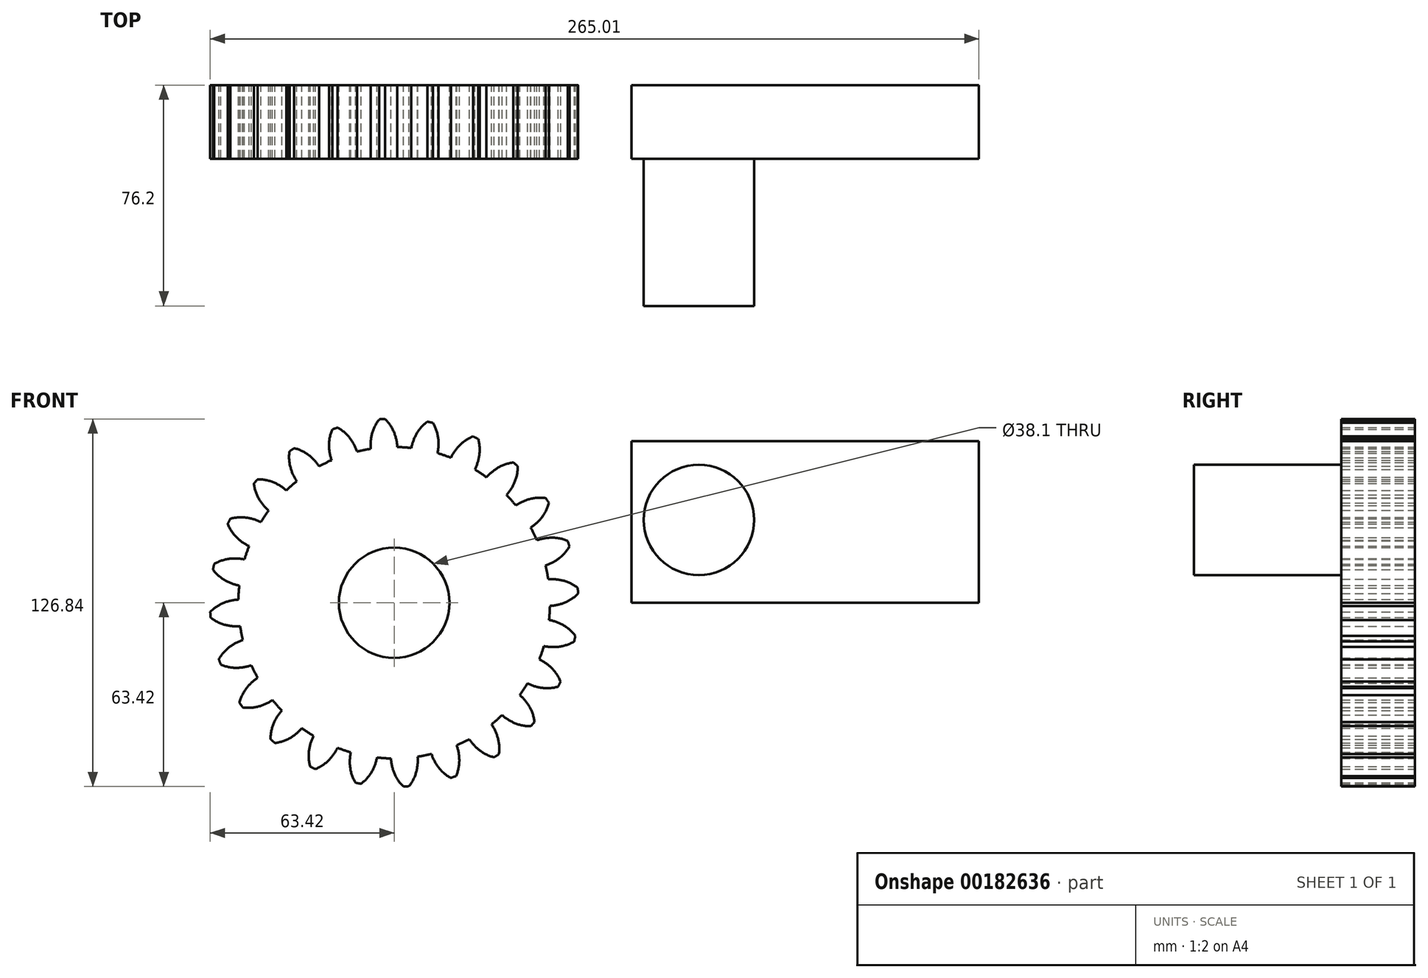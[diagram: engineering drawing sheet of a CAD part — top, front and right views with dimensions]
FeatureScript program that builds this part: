
annotation { "Feature Type Name" : "Feature", "Feature Type Description" : "" }
export const myFeature = defineFeature(function(context is Context, id is Id, definition is map)
    precondition{}
    {
        {
            var Q0;
            Q0=qCreatedBy(makeId("Front.planeOp"),FACE);
            var sketch = newSketch(context, id + "F0", { "sketchPlane" : qUnion([Q0])});
            skCircle(sketch, "E0", {"center": v(0, 0) * mm, "radius": 63.5 * mm, "construction": true});
            skCircle(sketch, "E1", {"center": v(0, 0) * mm, "radius": 58.67 * mm, "construction": true});
            skCircle(sketch, "E2", {"center": v(0, 0) * mm, "radius": 53.72 * mm});
            skLineSegment(sketch, "E3", {"start": v(0, 0) * mm, "end": v(0, 93.27) * mm, "construction": true});
            skLineSegment(sketch, "E4", {"start": v(0, 0) * mm, "end": v(-6.11, 93.27) * mm, "construction": true});
            skLineSegment(sketch, "E5", {"start": v(0, 58.67) * mm, "end": v(-115.99, 14.2) * mm, "construction": true});
            skLineSegment(sketch, "E6", {"start": v(-49.6, 39.66) * mm, "end": v(0, 58.67) * mm, "construction": true});
            skLineSegment(sketch, "E7", {"start": v(0, 58.67) * mm, "end": v(-118.86, 56.64) * mm, "construction": true});
            skCircle(sketch, "E8", {"center": v(0, 0) * mm, "radius": 54.78 * mm, "construction": true});
            skCircle(sketch, "E9", {"center": v(0, 58.67) * mm, "radius": 14.6 * mm, "construction": true});
            skCircle(sketch, "E10", {"center": v(-13.5, 53.1) * mm, "radius": 14.6 * mm, "construction": true});
            skArc(sketch, "E11", {"start": v(0, 58.67) * mm, "mid": v(-1.34, 61.21) * mm, "end": v(-3.17, 63.42) * mm});
            skArc(sketch, "E12", {"start": v(1.1, 53.7) * mm, "mid": v(0.75, 56.24) * mm, "end": v(0, 58.67) * mm});
            skArc(sketch, "E13.MirrorCS", {"start": v(-7.66, 58.17) * mm, "mid": v(-6.67, 60.86) * mm, "end": v(-5.14, 63.3) * mm});
            skArc(sketch, "E14.MirrorCS", {"start": v(-8.1, 53.1) * mm, "mid": v(-8.08, 55.66) * mm, "end": v(-7.66, 58.17) * mm});
            skArc(sketch, "E15", {"start": v(-3.17, 63.42) * mm, "mid": v(-4.15, 63.36) * mm, "end": v(-5.14, 63.3) * mm});
            skSolve(sketch);
        }
        {
            var Q0;
            {var subQ0=sQuery(id+"F0.wireOp",EDGE,"E2");var subQ1=makeQuery(id+"F0.imprint","INTERSECT",VERTEX,{"derivedFrom":[subQ0,sQuery(id+"F0.wireOp",EDGE,"E12")]});Q0=makeQuery(id+"F0.imprint","IMPRINT",FACE,{"disambiguationData":[TD([[makeQuery(id+"F0.imprint","IMPRINT",EDGE,{"disambiguationData":[TD([[subQ1,-1.0]])],"derivedFrom":subQ0}),1.0]])]});}
            var Q1;
            Q1=makeQuery(id+"F0.imprint","IMPRINT",FACE,{"disambiguationData":[TD([[makeQuery(id+"F0.imprint","IMPRINT",EDGE,{"derivedFrom":sQuery(id+"F0.wireOp",EDGE,"E11")}),1.0]])]});
            extrude(context, id + "F1", {"entities" : qUnion([Q0, Q1]), "depth" : 25.4 * mm});
        }
        {
            var Q0;
            Q0=makeQuery(id+"F1.opExtrude","SWEPT_BODY",BODY,{"disambiguationData":[OSD([sQuery(id+"F0.wireOp",EDGE,"E2"),sQuery(id+"F0.wireOp",EDGE,"E11"),sQuery(id+"F0.wireOp",EDGE,"E12"),sQuery(id+"F0.wireOp",EDGE,"E13.MirrorCS"),sQuery(id+"F0.wireOp",EDGE,"E14.MirrorCS"),sQuery(id+"F0.wireOp",EDGE,"E15")])]});
            var Q1;
            Q1=makeQuery(id+"F1.opExtrude","SWEPT_FACE",FACE,{"disambiguationData":[OSD([sQuery(id+"F0.wireOp",EDGE,"E2")])]});
            circularPattern(context, id + "F2", {"entities" : qUnion([Q0]), "axis" : qUnion([Q1]), "angle" : 15 * degree, "instanceCount" : 24});
        }
        {
            var Q0;
            Q0=makeQuery(id+"F2.opPattern","COPY",BODY,{"derivedFrom":makeQuery(id+"F1.opExtrude","SWEPT_BODY",BODY,{"disambiguationData":[OSD([sQuery(id+"F0.wireOp",EDGE,"E2"),sQuery(id+"F0.wireOp",EDGE,"E11"),sQuery(id+"F0.wireOp",EDGE,"E12"),sQuery(id+"F0.wireOp",EDGE,"E13.MirrorCS"),sQuery(id+"F0.wireOp",EDGE,"E14.MirrorCS"),sQuery(id+"F0.wireOp",EDGE,"E15")])]}),"instanceName":"9"});
            var Q1;
            Q1=makeQuery(id+"F2.opPattern","COPY",BODY,{"derivedFrom":makeQuery(id+"F1.opExtrude","SWEPT_BODY",BODY,{"disambiguationData":[OSD([sQuery(id+"F0.wireOp",EDGE,"E2"),sQuery(id+"F0.wireOp",EDGE,"E11"),sQuery(id+"F0.wireOp",EDGE,"E12"),sQuery(id+"F0.wireOp",EDGE,"E13.MirrorCS"),sQuery(id+"F0.wireOp",EDGE,"E14.MirrorCS"),sQuery(id+"F0.wireOp",EDGE,"E15")])]}),"instanceName":"23"});
            var Q2;
            Q2=makeQuery(id+"F2.opPattern","COPY",BODY,{"derivedFrom":makeQuery(id+"F1.opExtrude","SWEPT_BODY",BODY,{"disambiguationData":[OSD([sQuery(id+"F0.wireOp",EDGE,"E2"),sQuery(id+"F0.wireOp",EDGE,"E11"),sQuery(id+"F0.wireOp",EDGE,"E12"),sQuery(id+"F0.wireOp",EDGE,"E13.MirrorCS"),sQuery(id+"F0.wireOp",EDGE,"E14.MirrorCS"),sQuery(id+"F0.wireOp",EDGE,"E15")])]}),"instanceName":"22"});
            var Q3;
            Q3=makeQuery(id+"F2.opPattern","COPY",BODY,{"derivedFrom":makeQuery(id+"F1.opExtrude","SWEPT_BODY",BODY,{"disambiguationData":[OSD([sQuery(id+"F0.wireOp",EDGE,"E2"),sQuery(id+"F0.wireOp",EDGE,"E11"),sQuery(id+"F0.wireOp",EDGE,"E12"),sQuery(id+"F0.wireOp",EDGE,"E13.MirrorCS"),sQuery(id+"F0.wireOp",EDGE,"E14.MirrorCS"),sQuery(id+"F0.wireOp",EDGE,"E15")])]}),"instanceName":"21"});
            var Q4;
            Q4=makeQuery(id+"F2.opPattern","COPY",BODY,{"derivedFrom":makeQuery(id+"F1.opExtrude","SWEPT_BODY",BODY,{"disambiguationData":[OSD([sQuery(id+"F0.wireOp",EDGE,"E2"),sQuery(id+"F0.wireOp",EDGE,"E11"),sQuery(id+"F0.wireOp",EDGE,"E12"),sQuery(id+"F0.wireOp",EDGE,"E13.MirrorCS"),sQuery(id+"F0.wireOp",EDGE,"E14.MirrorCS"),sQuery(id+"F0.wireOp",EDGE,"E15")])]}),"instanceName":"20"});
            var Q5;
            Q5=makeQuery(id+"F2.opPattern","COPY",BODY,{"derivedFrom":makeQuery(id+"F1.opExtrude","SWEPT_BODY",BODY,{"disambiguationData":[OSD([sQuery(id+"F0.wireOp",EDGE,"E2"),sQuery(id+"F0.wireOp",EDGE,"E11"),sQuery(id+"F0.wireOp",EDGE,"E12"),sQuery(id+"F0.wireOp",EDGE,"E13.MirrorCS"),sQuery(id+"F0.wireOp",EDGE,"E14.MirrorCS"),sQuery(id+"F0.wireOp",EDGE,"E15")])]}),"instanceName":"16"});
            var Q6;
            Q6=makeQuery(id+"F2.opPattern","COPY",BODY,{"derivedFrom":makeQuery(id+"F1.opExtrude","SWEPT_BODY",BODY,{"disambiguationData":[OSD([sQuery(id+"F0.wireOp",EDGE,"E2"),sQuery(id+"F0.wireOp",EDGE,"E11"),sQuery(id+"F0.wireOp",EDGE,"E12"),sQuery(id+"F0.wireOp",EDGE,"E13.MirrorCS"),sQuery(id+"F0.wireOp",EDGE,"E14.MirrorCS"),sQuery(id+"F0.wireOp",EDGE,"E15")])]}),"instanceName":"18"});
            var Q7;
            Q7=makeQuery(id+"F2.opPattern","COPY",BODY,{"derivedFrom":makeQuery(id+"F1.opExtrude","SWEPT_BODY",BODY,{"disambiguationData":[OSD([sQuery(id+"F0.wireOp",EDGE,"E2"),sQuery(id+"F0.wireOp",EDGE,"E11"),sQuery(id+"F0.wireOp",EDGE,"E12"),sQuery(id+"F0.wireOp",EDGE,"E13.MirrorCS"),sQuery(id+"F0.wireOp",EDGE,"E14.MirrorCS"),sQuery(id+"F0.wireOp",EDGE,"E15")])]}),"instanceName":"17"});
            var Q8;
            Q8=makeQuery(id+"F2.opPattern","COPY",BODY,{"derivedFrom":makeQuery(id+"F1.opExtrude","SWEPT_BODY",BODY,{"disambiguationData":[OSD([sQuery(id+"F0.wireOp",EDGE,"E2"),sQuery(id+"F0.wireOp",EDGE,"E11"),sQuery(id+"F0.wireOp",EDGE,"E12"),sQuery(id+"F0.wireOp",EDGE,"E13.MirrorCS"),sQuery(id+"F0.wireOp",EDGE,"E14.MirrorCS"),sQuery(id+"F0.wireOp",EDGE,"E15")])]}),"instanceName":"19"});
            var Q9;
            Q9=makeQuery(id+"F2.opPattern","COPY",BODY,{"derivedFrom":makeQuery(id+"F1.opExtrude","SWEPT_BODY",BODY,{"disambiguationData":[OSD([sQuery(id+"F0.wireOp",EDGE,"E2"),sQuery(id+"F0.wireOp",EDGE,"E11"),sQuery(id+"F0.wireOp",EDGE,"E12"),sQuery(id+"F0.wireOp",EDGE,"E13.MirrorCS"),sQuery(id+"F0.wireOp",EDGE,"E14.MirrorCS"),sQuery(id+"F0.wireOp",EDGE,"E15")])]}),"instanceName":"15"});
            var Q10;
            Q10=makeQuery(id+"F2.opPattern","COPY",BODY,{"derivedFrom":makeQuery(id+"F1.opExtrude","SWEPT_BODY",BODY,{"disambiguationData":[OSD([sQuery(id+"F0.wireOp",EDGE,"E2"),sQuery(id+"F0.wireOp",EDGE,"E11"),sQuery(id+"F0.wireOp",EDGE,"E12"),sQuery(id+"F0.wireOp",EDGE,"E13.MirrorCS"),sQuery(id+"F0.wireOp",EDGE,"E14.MirrorCS"),sQuery(id+"F0.wireOp",EDGE,"E15")])]}),"instanceName":"14"});
            var Q11;
            Q11=makeQuery(id+"F2.opPattern","COPY",BODY,{"derivedFrom":makeQuery(id+"F1.opExtrude","SWEPT_BODY",BODY,{"disambiguationData":[OSD([sQuery(id+"F0.wireOp",EDGE,"E2"),sQuery(id+"F0.wireOp",EDGE,"E11"),sQuery(id+"F0.wireOp",EDGE,"E12"),sQuery(id+"F0.wireOp",EDGE,"E13.MirrorCS"),sQuery(id+"F0.wireOp",EDGE,"E14.MirrorCS"),sQuery(id+"F0.wireOp",EDGE,"E15")])]}),"instanceName":"12"});
            var Q12;
            Q12=makeQuery(id+"F2.opPattern","COPY",BODY,{"derivedFrom":makeQuery(id+"F1.opExtrude","SWEPT_BODY",BODY,{"disambiguationData":[OSD([sQuery(id+"F0.wireOp",EDGE,"E2"),sQuery(id+"F0.wireOp",EDGE,"E11"),sQuery(id+"F0.wireOp",EDGE,"E12"),sQuery(id+"F0.wireOp",EDGE,"E13.MirrorCS"),sQuery(id+"F0.wireOp",EDGE,"E14.MirrorCS"),sQuery(id+"F0.wireOp",EDGE,"E15")])]}),"instanceName":"13"});
            var Q13;
            Q13=makeQuery(id+"F2.opPattern","COPY",BODY,{"derivedFrom":makeQuery(id+"F1.opExtrude","SWEPT_BODY",BODY,{"disambiguationData":[OSD([sQuery(id+"F0.wireOp",EDGE,"E2"),sQuery(id+"F0.wireOp",EDGE,"E11"),sQuery(id+"F0.wireOp",EDGE,"E12"),sQuery(id+"F0.wireOp",EDGE,"E13.MirrorCS"),sQuery(id+"F0.wireOp",EDGE,"E14.MirrorCS"),sQuery(id+"F0.wireOp",EDGE,"E15")])]}),"instanceName":"11"});
            var Q14;
            Q14=makeQuery(id+"F2.opPattern","COPY",BODY,{"derivedFrom":makeQuery(id+"F1.opExtrude","SWEPT_BODY",BODY,{"disambiguationData":[OSD([sQuery(id+"F0.wireOp",EDGE,"E2"),sQuery(id+"F0.wireOp",EDGE,"E11"),sQuery(id+"F0.wireOp",EDGE,"E12"),sQuery(id+"F0.wireOp",EDGE,"E13.MirrorCS"),sQuery(id+"F0.wireOp",EDGE,"E14.MirrorCS"),sQuery(id+"F0.wireOp",EDGE,"E15")])]}),"instanceName":"10"});
            var Q15;
            Q15=makeQuery(id+"F2.opPattern","COPY",BODY,{"derivedFrom":makeQuery(id+"F1.opExtrude","SWEPT_BODY",BODY,{"disambiguationData":[OSD([sQuery(id+"F0.wireOp",EDGE,"E2"),sQuery(id+"F0.wireOp",EDGE,"E11"),sQuery(id+"F0.wireOp",EDGE,"E12"),sQuery(id+"F0.wireOp",EDGE,"E13.MirrorCS"),sQuery(id+"F0.wireOp",EDGE,"E14.MirrorCS"),sQuery(id+"F0.wireOp",EDGE,"E15")])]}),"instanceName":"8"});
            var Q16;
            Q16=makeQuery(id+"F2.opPattern","COPY",BODY,{"derivedFrom":makeQuery(id+"F1.opExtrude","SWEPT_BODY",BODY,{"disambiguationData":[OSD([sQuery(id+"F0.wireOp",EDGE,"E2"),sQuery(id+"F0.wireOp",EDGE,"E11"),sQuery(id+"F0.wireOp",EDGE,"E12"),sQuery(id+"F0.wireOp",EDGE,"E13.MirrorCS"),sQuery(id+"F0.wireOp",EDGE,"E14.MirrorCS"),sQuery(id+"F0.wireOp",EDGE,"E15")])]}),"instanceName":"7"});
            var Q17;
            Q17=makeQuery(id+"F2.opPattern","COPY",BODY,{"derivedFrom":makeQuery(id+"F1.opExtrude","SWEPT_BODY",BODY,{"disambiguationData":[OSD([sQuery(id+"F0.wireOp",EDGE,"E2"),sQuery(id+"F0.wireOp",EDGE,"E11"),sQuery(id+"F0.wireOp",EDGE,"E12"),sQuery(id+"F0.wireOp",EDGE,"E13.MirrorCS"),sQuery(id+"F0.wireOp",EDGE,"E14.MirrorCS"),sQuery(id+"F0.wireOp",EDGE,"E15")])]}),"instanceName":"6"});
            var Q18;
            Q18=makeQuery(id+"F2.opPattern","COPY",BODY,{"derivedFrom":makeQuery(id+"F1.opExtrude","SWEPT_BODY",BODY,{"disambiguationData":[OSD([sQuery(id+"F0.wireOp",EDGE,"E2"),sQuery(id+"F0.wireOp",EDGE,"E11"),sQuery(id+"F0.wireOp",EDGE,"E12"),sQuery(id+"F0.wireOp",EDGE,"E13.MirrorCS"),sQuery(id+"F0.wireOp",EDGE,"E14.MirrorCS"),sQuery(id+"F0.wireOp",EDGE,"E15")])]}),"instanceName":"5"});
            var Q19;
            Q19=makeQuery(id+"F2.opPattern","COPY",BODY,{"derivedFrom":makeQuery(id+"F1.opExtrude","SWEPT_BODY",BODY,{"disambiguationData":[OSD([sQuery(id+"F0.wireOp",EDGE,"E2"),sQuery(id+"F0.wireOp",EDGE,"E11"),sQuery(id+"F0.wireOp",EDGE,"E12"),sQuery(id+"F0.wireOp",EDGE,"E13.MirrorCS"),sQuery(id+"F0.wireOp",EDGE,"E14.MirrorCS"),sQuery(id+"F0.wireOp",EDGE,"E15")])]}),"instanceName":"4"});
            var Q20;
            Q20=makeQuery(id+"F2.opPattern","COPY",BODY,{"derivedFrom":makeQuery(id+"F1.opExtrude","SWEPT_BODY",BODY,{"disambiguationData":[OSD([sQuery(id+"F0.wireOp",EDGE,"E2"),sQuery(id+"F0.wireOp",EDGE,"E11"),sQuery(id+"F0.wireOp",EDGE,"E12"),sQuery(id+"F0.wireOp",EDGE,"E13.MirrorCS"),sQuery(id+"F0.wireOp",EDGE,"E14.MirrorCS"),sQuery(id+"F0.wireOp",EDGE,"E15")])]}),"instanceName":"2"});
            var Q21;
            Q21=makeQuery(id+"F2.opPattern","COPY",BODY,{"derivedFrom":makeQuery(id+"F1.opExtrude","SWEPT_BODY",BODY,{"disambiguationData":[OSD([sQuery(id+"F0.wireOp",EDGE,"E2"),sQuery(id+"F0.wireOp",EDGE,"E11"),sQuery(id+"F0.wireOp",EDGE,"E12"),sQuery(id+"F0.wireOp",EDGE,"E13.MirrorCS"),sQuery(id+"F0.wireOp",EDGE,"E14.MirrorCS"),sQuery(id+"F0.wireOp",EDGE,"E15")])]}),"instanceName":"3"});
            var Q22;
            Q22=makeQuery(id+"F2.opPattern","COPY",BODY,{"derivedFrom":makeQuery(id+"F1.opExtrude","SWEPT_BODY",BODY,{"disambiguationData":[OSD([sQuery(id+"F0.wireOp",EDGE,"E2"),sQuery(id+"F0.wireOp",EDGE,"E11"),sQuery(id+"F0.wireOp",EDGE,"E12"),sQuery(id+"F0.wireOp",EDGE,"E13.MirrorCS"),sQuery(id+"F0.wireOp",EDGE,"E14.MirrorCS"),sQuery(id+"F0.wireOp",EDGE,"E15")])]}),"instanceName":"1"});
            var Q23;
            Q23=makeQuery(id+"F1.opExtrude","SWEPT_BODY",BODY,{"disambiguationData":[OSD([sQuery(id+"F0.wireOp",EDGE,"E2"),sQuery(id+"F0.wireOp",EDGE,"E11"),sQuery(id+"F0.wireOp",EDGE,"E12"),sQuery(id+"F0.wireOp",EDGE,"E13.MirrorCS"),sQuery(id+"F0.wireOp",EDGE,"E14.MirrorCS"),sQuery(id+"F0.wireOp",EDGE,"E15")])]});
            booleanBodies(context, id + "F3", {"operationType" : BooleanOperationType.UNION, "tools" : qUnion([Q0, Q1, Q2, Q3, Q4, Q5, Q6, Q7, Q8, Q9, Q10, Q11, Q12, Q13, Q14, Q15, Q16, Q17, Q18, Q19, Q20, Q21, Q22, Q23])});
        }
        {
            var Q0;
            {var subQ0=makeQuery(id+"F1.opExtrude","CAP_FACE",FACE,{"disambiguationData":[OSD([sQuery(id+"F0.wireOp",EDGE,"E2"),sQuery(id+"F0.wireOp",EDGE,"E11"),sQuery(id+"F0.wireOp",EDGE,"E12"),sQuery(id+"F0.wireOp",EDGE,"E13.MirrorCS"),sQuery(id+"F0.wireOp",EDGE,"E14.MirrorCS"),sQuery(id+"F0.wireOp",EDGE,"E15")])],"isStart":true});Q0=makeQuery(id+"F3.opBoolean","MERGE",FACE,{"derivedFrom":[subQ0,makeQuery(id+"F2.opPattern","COPY",FACE,{"derivedFrom":subQ0,"instanceName":"1"}),makeQuery(id+"F2.opPattern","COPY",FACE,{"derivedFrom":subQ0,"instanceName":"2"}),makeQuery(id+"F2.opPattern","COPY",FACE,{"derivedFrom":subQ0,"instanceName":"3"}),makeQuery(id+"F2.opPattern","COPY",FACE,{"derivedFrom":subQ0,"instanceName":"4"}),makeQuery(id+"F2.opPattern","COPY",FACE,{"derivedFrom":subQ0,"instanceName":"5"}),makeQuery(id+"F2.opPattern","COPY",FACE,{"derivedFrom":subQ0,"instanceName":"6"}),makeQuery(id+"F2.opPattern","COPY",FACE,{"derivedFrom":subQ0,"instanceName":"7"}),makeQuery(id+"F2.opPattern","COPY",FACE,{"derivedFrom":subQ0,"instanceName":"8"}),makeQuery(id+"F2.opPattern","COPY",FACE,{"derivedFrom":subQ0,"instanceName":"9"}),makeQuery(id+"F2.opPattern","COPY",FACE,{"derivedFrom":subQ0,"instanceName":"10"}),makeQuery(id+"F2.opPattern","COPY",FACE,{"derivedFrom":subQ0,"instanceName":"11"}),makeQuery(id+"F2.opPattern","COPY",FACE,{"derivedFrom":subQ0,"instanceName":"12"}),makeQuery(id+"F2.opPattern","COPY",FACE,{"derivedFrom":subQ0,"instanceName":"13"}),makeQuery(id+"F2.opPattern","COPY",FACE,{"derivedFrom":subQ0,"instanceName":"14"}),makeQuery(id+"F2.opPattern","COPY",FACE,{"derivedFrom":subQ0,"instanceName":"15"}),makeQuery(id+"F2.opPattern","COPY",FACE,{"derivedFrom":subQ0,"instanceName":"16"}),makeQuery(id+"F2.opPattern","COPY",FACE,{"derivedFrom":subQ0,"instanceName":"17"}),makeQuery(id+"F2.opPattern","COPY",FACE,{"derivedFrom":subQ0,"instanceName":"18"}),makeQuery(id+"F2.opPattern","COPY",FACE,{"derivedFrom":subQ0,"instanceName":"19"}),makeQuery(id+"F2.opPattern","COPY",FACE,{"derivedFrom":subQ0,"instanceName":"20"}),makeQuery(id+"F2.opPattern","COPY",FACE,{"derivedFrom":subQ0,"instanceName":"21"}),makeQuery(id+"F2.opPattern","COPY",FACE,{"derivedFrom":subQ0,"instanceName":"22"}),makeQuery(id+"F2.opPattern","COPY",FACE,{"derivedFrom":subQ0,"instanceName":"23"})]});}
            var sketch = newSketch(context, id + "F4", { "sketchPlane" : qUnion([Q0])});
            skCircle(sketch, "E16", {"center": v(0, 0) * mm, "radius": 19.05 * mm});
            skSolve(sketch);
        }
        {
            var Q0;
            Q0=makeQuery(id+"F4.imprint","IMPRINT",FACE,{"disambiguationData":[TD([[makeQuery(id+"F4.imprint","IMPRINT",EDGE,{"derivedFrom":sQuery(id+"F4.wireOp",EDGE,"E16")}),1.0]])]});
            extrude(context, id + "F5", {"entities" : qUnion([Q0]), "operationType" : NewBodyOperationType.REMOVE, "endBound" : BoundingType.THROUGH_ALL, "oppositeDirection" : true, "depth" : 25.4 * mm});
        }
        {
            var Q0;
            Q0=qCreatedBy(makeId("Front.planeOp"),FACE);
            var sketch = newSketch(context, id + "F6", { "sketchPlane" : qUnion([Q0])});
            skLineSegment(sketch, "E17.bottom", {"start": v(81.78, 55.78) * mm, "end": v(201.6, 55.78) * mm});
            skLineSegment(sketch, "E17.top", {"start": v(81.78, 0) * mm, "end": v(201.6, 0) * mm});
            skLineSegment(sketch, "E17.left", {"start": v(81.78, 55.78) * mm, "end": v(81.78, 0) * mm});
            skLineSegment(sketch, "E17.right", {"start": v(201.6, 55.78) * mm, "end": v(201.6, 0) * mm});
            skCircle(sketch, "E18", {"center": v(105.05, 28.58) * mm, "radius": 19.05 * mm});
            skSolve(sketch);
        }
        {
            var Q0;
            Q0=makeQuery(id+"F6.imprint","IMPRINT",FACE,{"disambiguationData":[TD([[makeQuery(id+"F6.imprint","IMPRINT",EDGE,{"derivedFrom":sQuery(id+"F6.wireOp",EDGE,"E18")}),1.0]])]});
            var Q1;
            Q1=makeQuery(id+"F6.imprint","IMPRINT",FACE,{"disambiguationData":[TD([[makeQuery(id+"F6.imprint","IMPRINT",EDGE,{"derivedFrom":sQuery(id+"F6.wireOp",EDGE,"E17.bottom")}),-1.0]])]});
            extrude(context, id + "F7", {"entities" : qUnion([Q0, Q1]), "depth" : 25.4 * mm});
        }
        {
            var Q0;
            Q0=makeQuery(id+"F6.imprint","IMPRINT",FACE,{"disambiguationData":[TD([[makeQuery(id+"F6.imprint","IMPRINT",EDGE,{"derivedFrom":sQuery(id+"F6.wireOp",EDGE,"E18")}),1.0]])]});
            extrude(context, id + "F8", {"entities" : qUnion([Q0]), "operationType" : NewBodyOperationType.ADD, "depth" : 76.2 * mm});
        }
    });
